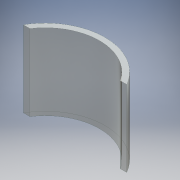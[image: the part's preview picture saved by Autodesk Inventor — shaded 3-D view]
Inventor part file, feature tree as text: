
AUTODESK INVENTOR PART (.ipt)
format: ipt  version: 2016 (Build 200138000, 138)  size: 98,816 bytes
history: native  units: mm
features: other x1, extrude x1, sketch x1
ambient origin geometry x8: Origin, YZ Plane, XZ Plane, XY Plane, X Axis, Y Axis, Z Axis, Center Point
bodies: Body1 (feature_tree)
feature tree (3):
  other  "ソリッド1"
  extrude  "押し出し1"  TaperAngle=30.0deg  [1 undecoded]
  sketch  "スケッチ1"
note: 1 required parameter value undecoded (feature->parameter linkage not recoverable at this tier; creation-order binding heuristic only, values carry confidence <= 0.55)
